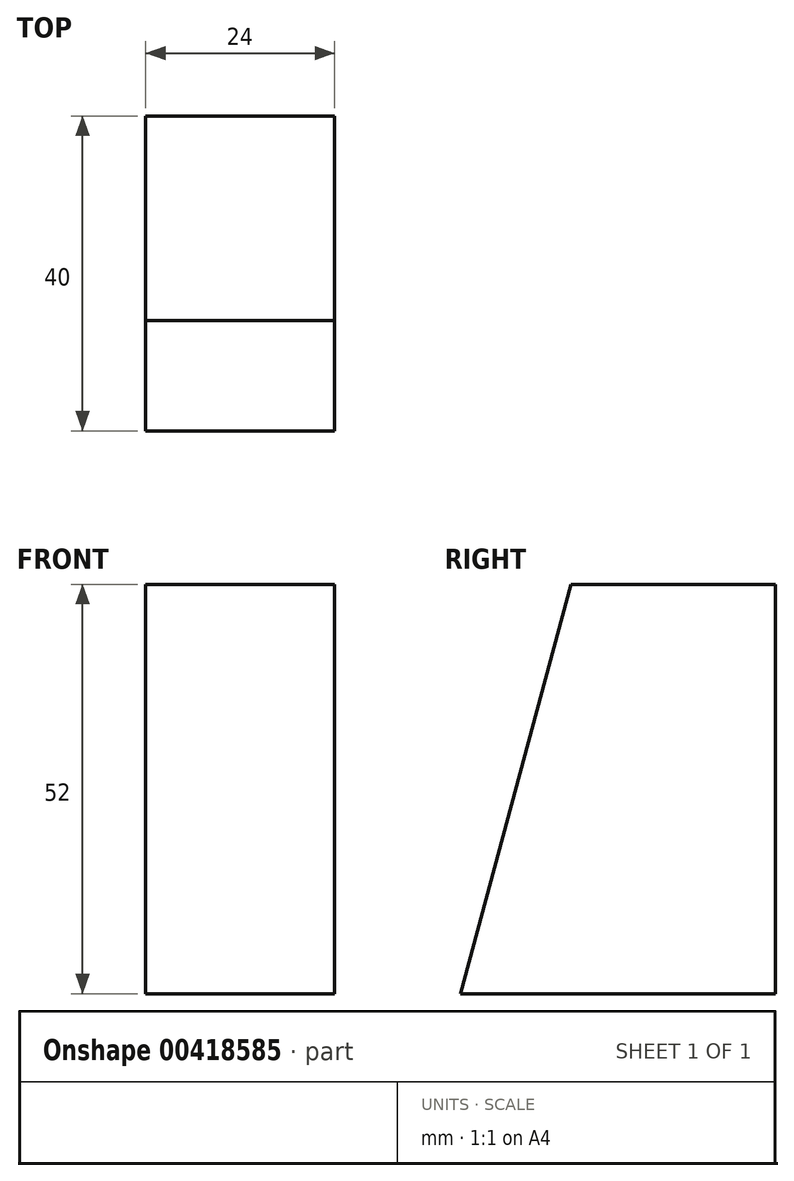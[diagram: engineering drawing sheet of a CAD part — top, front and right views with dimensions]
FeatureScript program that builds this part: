
annotation { "Feature Type Name" : "Feature", "Feature Type Description" : "" }
export const myFeature = defineFeature(function(context is Context, id is Id, definition is map)
    precondition{}
    {
        {
            var Q0;
            Q0=qCreatedBy(makeId("Right.planeOp"),FACE);
            var sketch = newSketch(context, id + "F0", { "sketchPlane" : qUnion([Q0])});
            skLineSegment(sketch, "E0", {"start": v(-26, 52) * mm, "end": v(0, 52) * mm});
            skLineSegment(sketch, "E1", {"start": v(0, 52) * mm, "end": v(0, 0) * mm});
            skLineSegment(sketch, "E2", {"start": v(0, 0) * mm, "end": v(-40, 0) * mm});
            skLineSegment(sketch, "E3", {"start": v(-40, 0) * mm, "end": v(-26, 52) * mm});
            skSolve(sketch);
        }
        {
            var Q0;
            Q0=makeQuery(id+"F0.imprint","IMPRINT",FACE,{"disambiguationData":[TD([[makeQuery(id+"F0.imprint","IMPRINT",EDGE,{"derivedFrom":sQuery(id+"F0.wireOp",EDGE,"E0")}),-1.0]])]});
            extrude(context, id + "F1", {"entities" : qUnion([Q0]), "depth" : 24 * mm});
        }
        {
            var Q0;
            Q0=qCreatedBy(makeId("Right.planeOp"),FACE);
            cPlane(context, id + "F2", {"entities" : qUnion([Q0]), "cplaneType" : CPlaneType.OFFSET, "offset" : 4 * mm, "width" : 150 * mm, "height" : 150 * mm});
        }
    });
